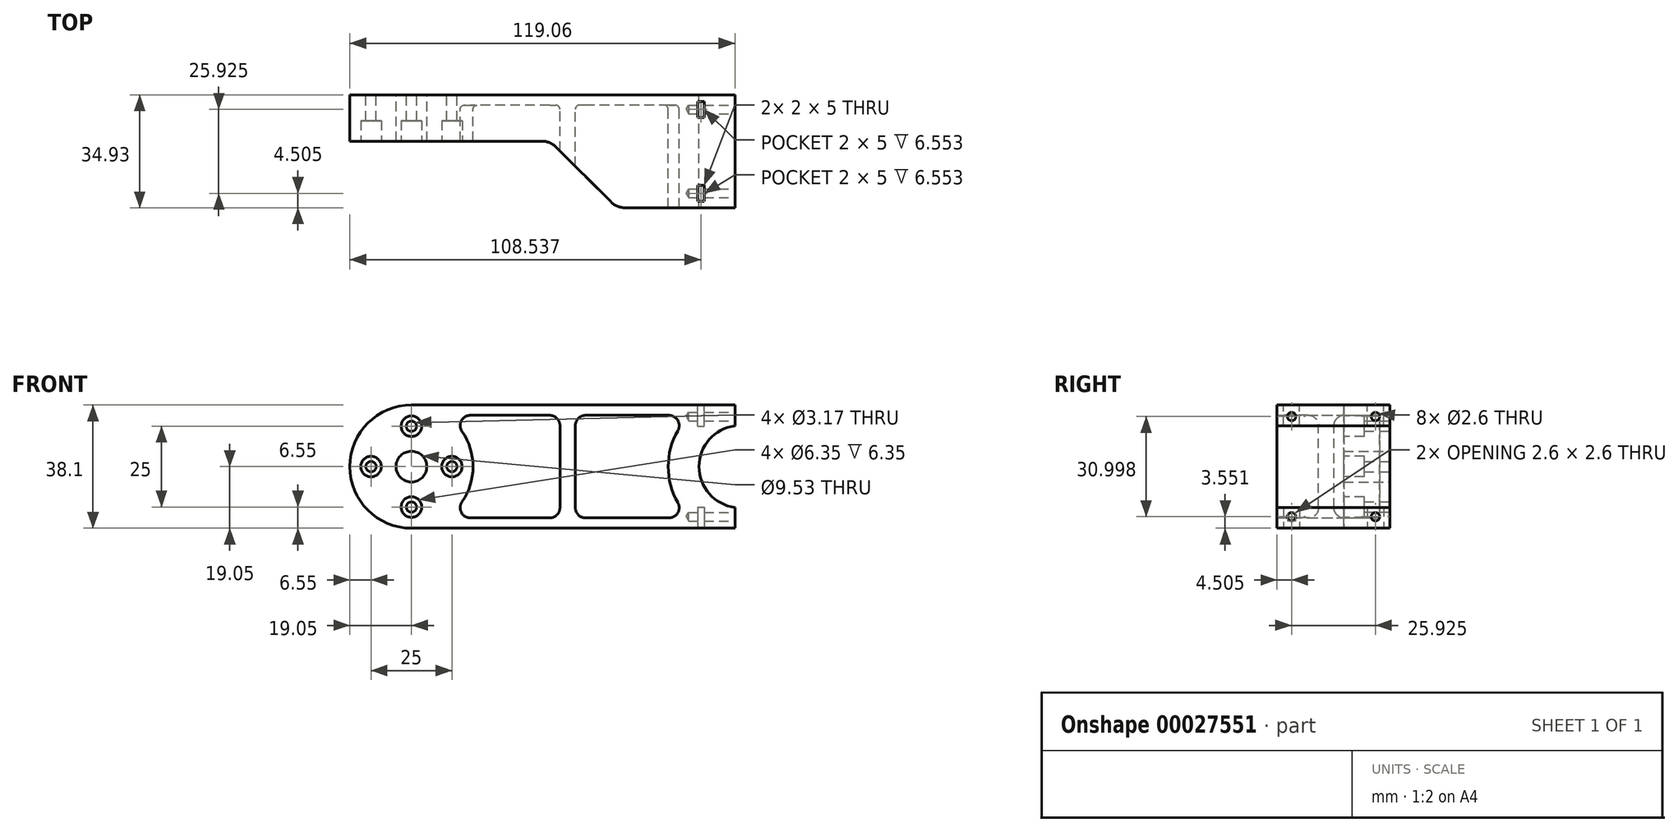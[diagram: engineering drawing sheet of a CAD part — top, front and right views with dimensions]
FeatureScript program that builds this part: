
annotation { "Feature Type Name" : "Feature", "Feature Type Description" : "" }
export const myFeature = defineFeature(function(context is Context, id is Id, definition is map)
    precondition{}
    {
        {
            var Q0;
            Q0=qCreatedBy(makeId("Front.planeOp"),FACE);
            var sketch = newSketch(context, id + "F0", { "sketchPlane" : qUnion([Q0])});
            skLineSegment(sketch, "E0", {"start": v(0, 23.47) * mm, "end": v(0, -23.47) * mm, "construction": true});
            skPoint(sketch, "E1", {"position": v(0, 0) * mm});
            skCircle(sketch, "E2", {"center": v(0, 0) * mm, "radius": 12.5 * mm, "construction": true});
            skLineSegment(sketch, "E3", {"start": v(0, 0) * mm, "end": v(101.6, 0) * mm, "construction": true});
            skArc(sketch, "E4", {"start": v(100.01, 12.6) * mm, "mid": v(88.9, 0) * mm, "end": v(100.01, -12.6) * mm});
            skLineSegment(sketch, "E5", {"start": v(101.6, 19.05) * mm, "end": v(101.6, -19.05) * mm, "construction": true});
            skLineSegment(sketch, "E6", {"start": v(100.01, 19.05) * mm, "end": v(100.01, 12.6) * mm});
            skArc(sketch, "E7", {"start": v(0, 19.05) * mm, "mid": v(-19.05, 0) * mm, "end": v(0, -19.05) * mm});
            skLineSegment(sketch, "E8", {"start": v(100.01, 19.05) * mm, "end": v(0, 19.05) * mm});
            skLineSegment(sketch, "E9", {"start": v(100.01, -19.05) * mm, "end": v(0, -19.05) * mm});
            skLineSegment(sketch, "E10.trimOffspring", {"start": v(100.01, -12.6) * mm, "end": v(100.01, -19.05) * mm});
            skLineSegment(sketch, "E11", {"start": v(0, 0) * mm, "end": v(8.84, 8.84) * mm, "construction": true});
            skSolve(sketch);
        }
        {
            var Q0;
            Q0 = qSketchRegion(id + "F0", true);
            extrude(context, id + "F1", {"entities" : qUnion([Q0]), "depth" : 34.92 * mm});
        }
        {
            var Q0;
            Q0=makeQuery(id+"F1.opExtrude","SWEPT_FACE",FACE,{"disambiguationData":[OSD([sQuery(id+"F0.wireOp",EDGE,"E8")])]});
            var sketch = newSketch(context, id + "F2", { "sketchPlane" : qUnion([Q0])});
            skLineSegment(sketch, "E12", {"start": v(-19.05, -14.29) * mm, "end": v(40.23, -14.29) * mm});
            skLineSegment(sketch, "E13", {"start": v(44.72, -16.15) * mm, "end": v(61.64, -33.07) * mm});
            skLineSegment(sketch, "E14", {"start": v(66.13, -34.93) * mm, "end": v(100.01, -34.93) * mm});
            skLineSegment(sketch, "E15", {"start": v(100.01, -34.93) * mm, "end": v(100.01, -38.1) * mm});
            skLineSegment(sketch, "E16", {"start": v(100.01, -38.1) * mm, "end": v(-19.05, -38.1) * mm});
            skLineSegment(sketch, "E17", {"start": v(-19.05, -34.92) * mm, "end": v(-19.05, -14.29) * mm});
            skLineSegment(sketch, "E18", {"start": v(-19.05, -34.92) * mm, "end": v(-19.05, -38.1) * mm});
            skPoint(sketch, "E19.visualSharp", {"position": v(42.86, -14.29) * mm});
            skArc(sketch, "E19.filletArc", {"start": v(44.72, -16.15) * mm, "mid": v(42.66, -14.77) * mm, "end": v(40.23, -14.29) * mm});
            skPoint(sketch, "E20.visualSharp", {"position": v(63.5, -34.93) * mm});
            skArc(sketch, "E20.filletArc", {"start": v(61.64, -33.07) * mm, "mid": v(63.7, -34.44) * mm, "end": v(66.13, -34.92) * mm});
            skSolve(sketch);
        }
        {
            var Q0;
            Q0 = qSketchRegion(id + "F2", true);
            extrude(context, id + "F3", {"entities" : qUnion([Q0]), "operationType" : NewBodyOperationType.REMOVE, "endBound" : BoundingType.THROUGH_ALL, "oppositeDirection" : true, "depth" : 25.4 * mm});
        }
        {
            var Q0;
            Q0=qCreatedBy(makeId("Front.planeOp"),FACE);
            cPlane(context, id + "F4", {"entities" : qUnion([Q0]), "cplaneType" : CPlaneType.OFFSET, "offset" : 3.17 * mm, "width" : 152.4 * mm, "height" : 152.4 * mm});
        }
        {
            var Q0;
            Q0=qCreatedBy(id+"F4.planeOp",FACE);
            var sketch = newSketch(context, id + "F5", { "sketchPlane" : qUnion([Q0])});
            skArc(sketch, "E21.0", {"start": v(82.35, 11.11) * mm, "mid": v(79.38, 0) * mm, "end": v(82.35, -11.11) * mm});
            skLineSegment(sketch, "E22", {"start": v(79.6, 15.88) * mm, "end": v(53.84, 15.88) * mm});
            skArc(sketch, "E23", {"start": v(15.63, -10.89) * mm, "mid": v(19.05, 0) * mm, "end": v(15.63, 10.89) * mm});
            skLineSegment(sketch, "E24", {"start": v(79.6, -15.87) * mm, "end": v(53.84, -15.88) * mm});
            skLineSegment(sketch, "E25", {"start": v(48.29, 19.05) * mm, "end": v(48.29, -19.05) * mm, "construction": true});
            skPoint(sketch, "E26", {"position": v(48.29, 15.88) * mm});
            skLineSegment(sketch, "E27.0", {"start": v(45.9, 12.7) * mm, "end": v(45.9, -12.7) * mm});
            skLineSegment(sketch, "E28.0", {"start": v(50.67, 12.7) * mm, "end": v(50.67, -12.7) * mm});
            skLineSegment(sketch, "E29.trimOffspring", {"start": v(42.73, 15.88) * mm, "end": v(18.24, 15.88) * mm});
            skLineSegment(sketch, "E30.trimOffspring", {"start": v(42.73, -15.88) * mm, "end": v(18.24, -15.88) * mm});
            skPoint(sketch, "E31.visualSharp", {"position": v(10.53, 15.88) * mm});
            skArc(sketch, "E31.filletArc", {"start": v(18.24, 15.88) * mm, "mid": v(15.42, 14.17) * mm, "end": v(15.63, 10.89) * mm});
            skPoint(sketch, "E32.visualSharp", {"position": v(10.53, -15.88) * mm});
            skArc(sketch, "E32.filletArc", {"start": v(15.63, -10.89) * mm, "mid": v(15.42, -14.17) * mm, "end": v(18.24, -15.88) * mm});
            skPoint(sketch, "E33.visualSharp", {"position": v(86.05, -15.88) * mm});
            skArc(sketch, "E33.filletArc", {"start": v(79.6, -15.87) * mm, "mid": v(82.35, -14.29) * mm, "end": v(82.35, -11.11) * mm});
            skPoint(sketch, "E34.visualSharp", {"position": v(86.05, 15.88) * mm});
            skArc(sketch, "E34.filletArc", {"start": v(82.35, 11.11) * mm, "mid": v(82.35, 14.29) * mm, "end": v(79.6, 15.87) * mm});
            skPoint(sketch, "E35.visualSharp", {"position": v(45.9, 15.88) * mm});
            skArc(sketch, "E35.filletArc", {"start": v(45.9, 12.7) * mm, "mid": v(44.98, 14.95) * mm, "end": v(42.73, 15.88) * mm});
            skPoint(sketch, "E36.visualSharp", {"position": v(45.9, -15.88) * mm});
            skArc(sketch, "E36.filletArc", {"start": v(42.73, -15.88) * mm, "mid": v(44.98, -14.95) * mm, "end": v(45.9, -12.7) * mm});
            skPoint(sketch, "E37.visualSharp", {"position": v(50.67, 15.88) * mm});
            skArc(sketch, "E37.filletArc", {"start": v(53.84, 15.88) * mm, "mid": v(51.6, 14.95) * mm, "end": v(50.67, 12.7) * mm});
            skPoint(sketch, "E38.visualSharp", {"position": v(50.67, -15.88) * mm});
            skArc(sketch, "E38.filletArc", {"start": v(50.67, -12.7) * mm, "mid": v(51.6, -14.95) * mm, "end": v(53.84, -15.88) * mm});
            skSolve(sketch);
        }
        {
            var Q0;
            Q0 = qSketchRegion(id + "F5", true);
            var Q1;
            Q1=makeQuery(id+"F1.opExtrude","CAP_FACE",FACE,{"disambiguationData":[OSD([sQuery(id+"F0.wireOp",EDGE,"E4"),sQuery(id+"F0.wireOp",EDGE,"E6"),sQuery(id+"F0.wireOp",EDGE,"E7"),sQuery(id+"F0.wireOp",EDGE,"E8"),sQuery(id+"F0.wireOp",EDGE,"E9"),sQuery(id+"F0.wireOp",EDGE,"E10.trimOffspring")])],"isStart":false});
            extrude(context, id + "F6", {"entities" : qUnion([Q0]), "operationType" : NewBodyOperationType.REMOVE, "endBound" : BoundingType.UP_TO_SURFACE, "endBoundEntityFace" : qUnion([Q1]), "depth" : 25.4 * mm});
        }
        {
            var Q0;
            Q0=makeQuery(id+"F6.boolean.opBoolean","COPY",EDGE,{"derivedFrom":makeQuery(id+"F6.opExtrude","CAP_EDGE",EDGE,{"disambiguationData":[OSD([sQuery(id+"F5.wireOp",EDGE,"E23")])],"isStart":true})});
            var Q1;
            Q1=makeQuery(id+"F6.boolean.opBoolean","COPY",EDGE,{"derivedFrom":makeQuery(id+"F6.opExtrude","CAP_EDGE",EDGE,{"disambiguationData":[OSD([sQuery(id+"F5.wireOp",EDGE,"E28.0")])],"isStart":true})});
            fillet(context, id + "F7", {"entities" : qUnion([Q0, Q1]), "radius" : 1.27 * mm, "tangentPropagation" : true, "allowEdgeOverflow" : false});
        }
        {
            var Q0;
            Q0=makeQuery(id+"F1.opExtrude","CAP_FACE",FACE,{"disambiguationData":[OSD([sQuery(id+"F0.wireOp",EDGE,"E4"),sQuery(id+"F0.wireOp",EDGE,"E6"),sQuery(id+"F0.wireOp",EDGE,"E7"),sQuery(id+"F0.wireOp",EDGE,"E8"),sQuery(id+"F0.wireOp",EDGE,"E9"),sQuery(id+"F0.wireOp",EDGE,"E10.trimOffspring")])],"isStart":true});
            var sketch = newSketch(context, id + "F8", { "sketchPlane" : qUnion([Q0])});
            skCircle(sketch, "E39", {"center": v(0, 0) * mm, "radius": 12.5 * mm, "construction": true});
            skLineSegment(sketch, "E40", {"start": v(0, 0) * mm, "end": v(12.5, 0) * mm, "construction": true});
            skCircle(sketch, "E41", {"center": v(12.5, 0) * mm, "radius": 1.59 * mm});
            skCircle(sketch, "E42.1.0", {"center": v(0, 12.5) * mm, "radius": 1.59 * mm});
            skCircle(sketch, "E42.2.0", {"center": v(-12.5, 0) * mm, "radius": 1.59 * mm});
            skCircle(sketch, "E42.3.0", {"center": v(0, -12.5) * mm, "radius": 1.59 * mm});
            skCircle(sketch, "E43", {"center": v(0, 0) * mm, "radius": 4.76 * mm});
            skSolve(sketch);
        }
        {
            var Q0;
            Q0 = qSketchRegion(id + "F8", true);
            extrude(context, id + "F9", {"entities" : qUnion([Q0]), "operationType" : NewBodyOperationType.REMOVE, "endBound" : BoundingType.THROUGH_ALL, "oppositeDirection" : true, "depth" : 25.4 * mm});
        }
        {
            var Q0;
            Q0=makeQuery(id+"F3.boolean.opBoolean","COPY",FACE,{"derivedFrom":makeQuery(id+"F3.opExtrude","SWEPT_FACE",FACE,{"disambiguationData":[OSD([sQuery(id+"F2.wireOp",EDGE,"E12")])]})});
            var sketch = newSketch(context, id + "F10", { "sketchPlane" : qUnion([Q0])});
            skCircle(sketch, "E44", {"center": v(-12.5, 0) * mm, "radius": 3.18 * mm});
            skCircle(sketch, "E45", {"center": v(0, 12.5) * mm, "radius": 3.18 * mm});
            skCircle(sketch, "E46", {"center": v(12.5, 0) * mm, "radius": 3.18 * mm});
            skCircle(sketch, "E47", {"center": v(0, -12.5) * mm, "radius": 3.18 * mm});
            skSolve(sketch);
        }
        {
            var Q0;
            Q0 = qSketchRegion(id + "F10", true);
            extrude(context, id + "F11", {"entities" : qUnion([Q0]), "operationType" : NewBodyOperationType.REMOVE, "oppositeDirection" : true, "depth" : 6.35 * mm});
        }
        {
            var Q0;
            Q0=makeQuery(id+"F1.opExtrude","SWEPT_FACE",FACE,{"disambiguationData":[OSD([sQuery(id+"F0.wireOp",EDGE,"E6")])]});
            var sketch = newSketch(context, id + "F12", { "sketchPlane" : qUnion([Q0])});
            skLineSegment(sketch, "E48", {"start": v(0, 0) * mm, "end": v(-34.93, 0) * mm, "construction": true});
            skLineSegment(sketch, "E49.0", {"start": v(0, 15.5) * mm, "end": v(-34.93, 15.5) * mm, "construction": true});
            skPoint(sketch, "E50", {"position": v(-30.43, 15.5) * mm});
            skPoint(sketch, "E51", {"position": v(-4.5, 15.5) * mm});
            skPoint(sketch, "E52.MirrorP", {"position": v(-4.5, -15.5) * mm});
            skPoint(sketch, "E53.MirrorP", {"position": v(-30.43, -15.5) * mm});
            skSolve(sketch);
        }
        {
            var Q0;
            Q0=sQuery(id+"F12.wireOp",VERTEX,"E50");
            var Q1;
            Q1=sQuery(id+"F12.wireOp",VERTEX,"E51");
            var Q2;
            Q2=sQuery(id+"F12.wireOp",VERTEX,"E53.MirrorP");
            var Q3;
            Q3=sQuery(id+"F12.wireOp",VERTEX,"E52.MirrorP");
            var Q4;
            Q4=makeQuery(id+"F1.opExtrude","SWEPT_BODY",BODY,{"disambiguationData":[OSD([sQuery(id+"F0.wireOp",EDGE,"E4"),sQuery(id+"F0.wireOp",EDGE,"E6"),sQuery(id+"F0.wireOp",EDGE,"E7"),sQuery(id+"F0.wireOp",EDGE,"E8"),sQuery(id+"F0.wireOp",EDGE,"E9"),sQuery(id+"F0.wireOp",EDGE,"E10.trimOffspring")])]});
            hole(context, id + "F13", {"style" : HoleStyle.SIMPLE, "holeDiameter" : 2.6 * mm, "endStyle" : HoleEndStyle.BLIND, "holeDepth" : 14.29 * mm, "locations" : qUnion([Q0, Q1, Q2, Q3]), "scope" : qUnion([Q4])});
        }
        {
            var Q0;
            Q0=makeQuery(id+"F1.opExtrude","SWEPT_FACE",FACE,{"disambiguationData":[OSD([sQuery(id+"F0.wireOp",EDGE,"E8")])]});
            var sketch = newSketch(context, id + "F14", { "sketchPlane" : qUnion([Q0])});
            skLineSegment(sketch, "E54.0", {"start": v(90.49, -32.93) * mm, "end": v(90.49, -27.93) * mm});
            skLineSegment(sketch, "E55.0", {"start": v(88.49, -32.93) * mm, "end": v(88.49, -27.93) * mm});
            skLineSegment(sketch, "E56", {"start": v(85.73, -4.5) * mm, "end": v(100.01, -4.5) * mm, "construction": true});
            skLineSegment(sketch, "E57", {"start": v(85.73, -30.43) * mm, "end": v(100.01, -30.43) * mm, "construction": true});
            skLineSegment(sketch, "E58.0", {"start": v(88.49, -7) * mm, "end": v(90.49, -7) * mm});
            skLineSegment(sketch, "E59.0", {"start": v(88.49, -2) * mm, "end": v(90.49, -2) * mm});
            skLineSegment(sketch, "E60.0", {"start": v(88.49, -32.93) * mm, "end": v(90.49, -32.93) * mm});
            skLineSegment(sketch, "E61.0", {"start": v(88.49, -27.93) * mm, "end": v(90.49, -27.93) * mm});
            skLineSegment(sketch, "E62.trimOffspring", {"start": v(88.49, -7) * mm, "end": v(88.49, -2) * mm});
            skLineSegment(sketch, "E63.trimOffspring", {"start": v(90.49, -7) * mm, "end": v(90.49, -2) * mm});
            skSolve(sketch);
        }
        {
            var Q0;
            Q0 = qSketchRegion(id + "F14", true);
            extrude(context, id + "F15", {"entities" : qUnion([Q0]), "operationType" : NewBodyOperationType.REMOVE, "oppositeDirection" : true, "depth" : 6.55 * mm});
        }
        {
            var Q0;
            Q0=makeQuery(id+"F1.opExtrude","SWEPT_FACE",FACE,{"disambiguationData":[OSD([sQuery(id+"F0.wireOp",EDGE,"E9")])]});
            var sketch = newSketch(context, id + "F16", { "sketchPlane" : qUnion([Q0])});
            skLineSegment(sketch, "E64.0", {"start": v(88.49, 32.93) * mm, "end": v(88.49, 27.93) * mm});
            skLineSegment(sketch, "E65.0", {"start": v(88.49, 32.93) * mm, "end": v(90.49, 32.93) * mm});
            skLineSegment(sketch, "E66.0", {"start": v(90.49, 32.93) * mm, "end": v(90.49, 27.93) * mm});
            skLineSegment(sketch, "E67.0", {"start": v(88.49, 27.93) * mm, "end": v(90.49, 27.93) * mm});
            skLineSegment(sketch, "E68.0", {"start": v(85.73, 30.43) * mm, "end": v(100.01, 30.43) * mm, "construction": true});
            skLineSegment(sketch, "E69.0", {"start": v(85.73, 4.5) * mm, "end": v(100.01, 4.5) * mm, "construction": true});
            skLineSegment(sketch, "E70.0", {"start": v(88.49, 7) * mm, "end": v(88.49, 2) * mm});
            skLineSegment(sketch, "E71.0", {"start": v(88.49, 7) * mm, "end": v(90.49, 7) * mm});
            skLineSegment(sketch, "E72.0", {"start": v(90.49, 7) * mm, "end": v(90.49, 2) * mm});
            skLineSegment(sketch, "E73.0", {"start": v(88.49, 2) * mm, "end": v(90.49, 2) * mm});
            skSolve(sketch);
        }
        {
            var Q0;
            Q0 = qSketchRegion(id + "F16", true);
            extrude(context, id + "F17", {"entities" : qUnion([Q0]), "operationType" : NewBodyOperationType.REMOVE, "oppositeDirection" : true, "depth" : 6.55 * mm});
        }
    });
